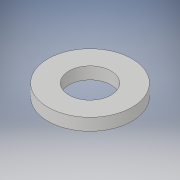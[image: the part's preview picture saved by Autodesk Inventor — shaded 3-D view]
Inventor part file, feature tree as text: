
AUTODESK INVENTOR PART (.ipt)
format: ipt  version: 2017 (Build 210142000, 142)  size: 97,792 bytes
history: native  units: in
note: dims shown in document units (in); Inventor stores cm internally (conversion verified against a paired STEP export)
features: extrude x1, hole x1, sketch x1
ambient origin geometry x8: Origin, YZ Plane, XZ Plane, XY Plane, X Axis, Y Axis, Z Axis, Center Point
bodies: Solid1 (feature_tree)
feature tree (3):
  extrude  "Extrusion1"  Depth=0.09in TaperAngle=0.0deg
  hole  "Hole1"  [1 undecoded]
  sketch  "Sketch1"  dims[d0=0.625in d1=0.09in d2=0.0in d3=1.0in d4=1.0in d5=0.3125in d6=0.75in d7=0.375in d8=0.25in d9=0.5635in d10=0.3125in d11=0.8108in]
note: 1 required parameter value undecoded (feature->parameter linkage not recoverable at this tier; creation-order binding heuristic only, values carry confidence <= 0.55)
